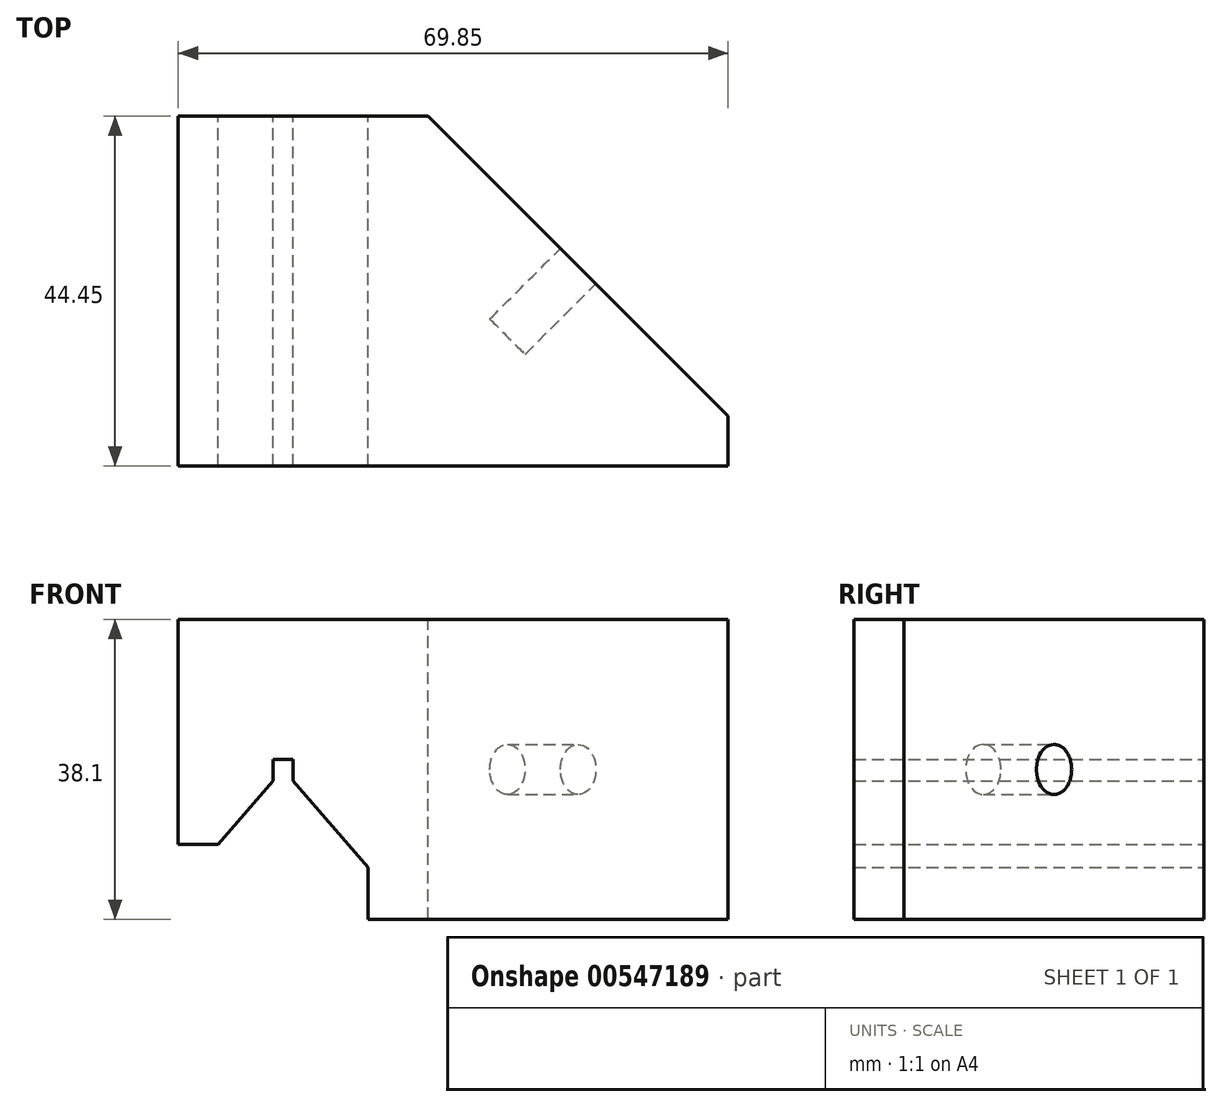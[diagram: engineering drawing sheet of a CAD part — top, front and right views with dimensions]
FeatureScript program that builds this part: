
annotation { "Feature Type Name" : "Feature", "Feature Type Description" : "" }
export const myFeature = defineFeature(function(context is Context, id is Id, definition is map)
    precondition{}
    {
        {
            var Q0;
            Q0=qCreatedBy(makeId("Front.planeOp"),FACE);
            var sketch = newSketch(context, id + "F0", { "sketchPlane" : qUnion([Q0])});
            skLineSegment(sketch, "E0.bottom", {"start": v(0, 0) * mm, "end": v(69.85, 0) * mm});
            skLineSegment(sketch, "E0.top", {"start": v(0, 38.1) * mm, "end": v(69.85, 38.1) * mm});
            skLineSegment(sketch, "E0.left", {"start": v(0, 0) * mm, "end": v(0, 38.1) * mm});
            skLineSegment(sketch, "E0.right", {"start": v(69.85, 0) * mm, "end": v(69.85, 38.1) * mm});
            skLineSegment(sketch, "E1", {"start": v(0, 9.53) * mm, "end": v(5.08, 9.53) * mm, "construction": true});
            skLineSegment(sketch, "E2", {"start": v(0, 19.05) * mm, "end": v(12.07, 19.05) * mm, "construction": true});
            skLineSegment(sketch, "E3", {"start": v(5.08, 38.1) * mm, "end": v(5.08, 9.53) * mm, "construction": true});
            skLineSegment(sketch, "E4", {"start": v(21.6, 38.1) * mm, "end": v(21.6, 9.53) * mm, "construction": true});
            skLineSegment(sketch, "E5", {"start": v(24.13, 38.1) * mm, "end": v(24.13, 0) * mm, "construction": true});
            skLineSegment(sketch, "E6", {"start": v(13.34, 38.1) * mm, "end": v(13.34, 20.32) * mm, "construction": true});
            skLineSegment(sketch, "E7", {"start": v(12.06, 38.1) * mm, "end": v(12.07, 19.05) * mm, "construction": true});
            skLineSegment(sketch, "E8", {"start": v(14.6, 38.1) * mm, "end": v(14.6, 19.05) * mm, "construction": true});
            skLineSegment(sketch, "E9", {"start": v(0, 20.32) * mm, "end": v(21.6, 20.32) * mm, "construction": true});
            skLineSegment(sketch, "E10", {"start": v(0, 9.53) * mm, "end": v(5.08, 9.53) * mm});
            skLineSegment(sketch, "E11", {"start": v(5.08, 9.53) * mm, "end": v(12.07, 17.58) * mm});
            skLineSegment(sketch, "E12", {"start": v(14.6, 17.58) * mm, "end": v(21.6, 9.53) * mm});
            skLineSegment(sketch, "E13", {"start": v(21.6, 9.53) * mm, "end": v(24.13, 6.6) * mm});
            skLineSegment(sketch, "E14", {"start": v(24.13, 6.6) * mm, "end": v(24.13, 0) * mm});
            skLineSegment(sketch, "E15", {"start": v(14.6, 19.05) * mm, "end": v(14.6, 20.32) * mm});
            skLineSegment(sketch, "E16", {"start": v(14.6, 20.32) * mm, "end": v(12.07, 20.32) * mm});
            skLineSegment(sketch, "E17", {"start": v(12.07, 20.32) * mm, "end": v(12.07, 19.05) * mm});
            skLineSegment(sketch, "E18", {"start": v(12.07, 19.05) * mm, "end": v(12.07, 17.58) * mm});
            skLineSegment(sketch, "E19", {"start": v(14.6, 19.05) * mm, "end": v(14.6, 17.58) * mm});
            skLineSegment(sketch, "E20.trimOffspring", {"start": v(14.6, 19.05) * mm, "end": v(69.85, 19.05) * mm, "construction": true});
            skPoint(sketch, "E21.orphan", {"position": v(13.34, 19.05) * mm});
            skLineSegment(sketch, "E22.trimOffspring", {"start": v(21.6, 9.53) * mm, "end": v(69.85, 9.53) * mm, "construction": true});
            skPoint(sketch, "E23.orphan", {"position": v(21.6, 0) * mm});
            skPoint(sketch, "E24.orphan", {"position": v(5.08, 0) * mm});
            skSolve(sketch);
        }
        {
            var Q0;
            {var subQ4=sQuery(id+"F0.wireOp",EDGE,"E0.top");Q0=makeQuery(id+"F0.imprint","IMPRINT",FACE,{"disambiguationData":[TD([[makeQuery(id+"F0.imprint","IMPRINT",EDGE,{"derivedFrom":subQ4}),-1.0]])]});}
            extrude(context, id + "F1", {"entities" : qUnion([Q0]), "depth" : 44.45 * mm, "offsetDistance" : 25.4 * mm});
        }
        {
            var Q0;
            Q0=makeQuery(id+"F1.opExtrude","SWEPT_FACE",FACE,{"disambiguationData":[OSD([sQuery(id+"F0.wireOp",EDGE,"E0.top")])]});
            var sketch = newSketch(context, id + "F2", { "sketchPlane" : qUnion([Q0])});
            skLineSegment(sketch, "E25", {"start": v(69.85, 0) * mm, "end": v(69.85, -38.1) * mm});
            skLineSegment(sketch, "E26", {"start": v(69.85, 0) * mm, "end": v(31.75, 0) * mm});
            skLineSegment(sketch, "E27", {"start": v(69.85, -38.1) * mm, "end": v(31.75, 0) * mm});
            skSolve(sketch);
        }
        {
            var Q0;
            Q0=makeQuery(id+"F2.imprint","IMPRINT",FACE,{"disambiguationData":[TD([[makeQuery(id+"F2.imprint","IMPRINT",EDGE,{"derivedFrom":sQuery(id+"F2.wireOp",EDGE,"E25")}),1.0]])]});
            extrude(context, id + "F3", {"entities" : qUnion([Q0]), "operationType" : NewBodyOperationType.REMOVE, "oppositeDirection" : true, "depth" : 38.1 * mm, "offsetDistance" : 25.4 * mm});
        }
        {
            var Q0;
            Q0=makeQuery(id+"F3.boolean.opBoolean","COPY",FACE,{"derivedFrom":makeQuery(id+"F3.opExtrude","SWEPT_FACE",FACE,{"disambiguationData":[OSD([sQuery(id+"F2.wireOp",EDGE,"E27")])]})});
            var sketch = newSketch(context, id + "F4", { "sketchPlane" : qUnion([Q0])});
            skLineSegment(sketch, "E28", {"start": v(-76.33, 19.05) * mm, "end": v(-22.45, 19.05) * mm});
            skLineSegment(sketch, "E29", {"start": v(-49.4, 38.1) * mm, "end": v(-49.4, 0) * mm});
            skCircle(sketch, "E30", {"center": v(-49.4, 19.05) * mm, "radius": 3.18 * mm});
            skSolve(sketch);
        }
        {
            var Q0;
            Q0 = qSketchRegion(id + "F4", true);
            extrude(context, id + "F5", {"entities" : qUnion([Q0]), "operationType" : NewBodyOperationType.REMOVE, "oppositeDirection" : true, "depth" : 12.7 * mm, "offsetDistance" : 25.4 * mm});
        }
    });
